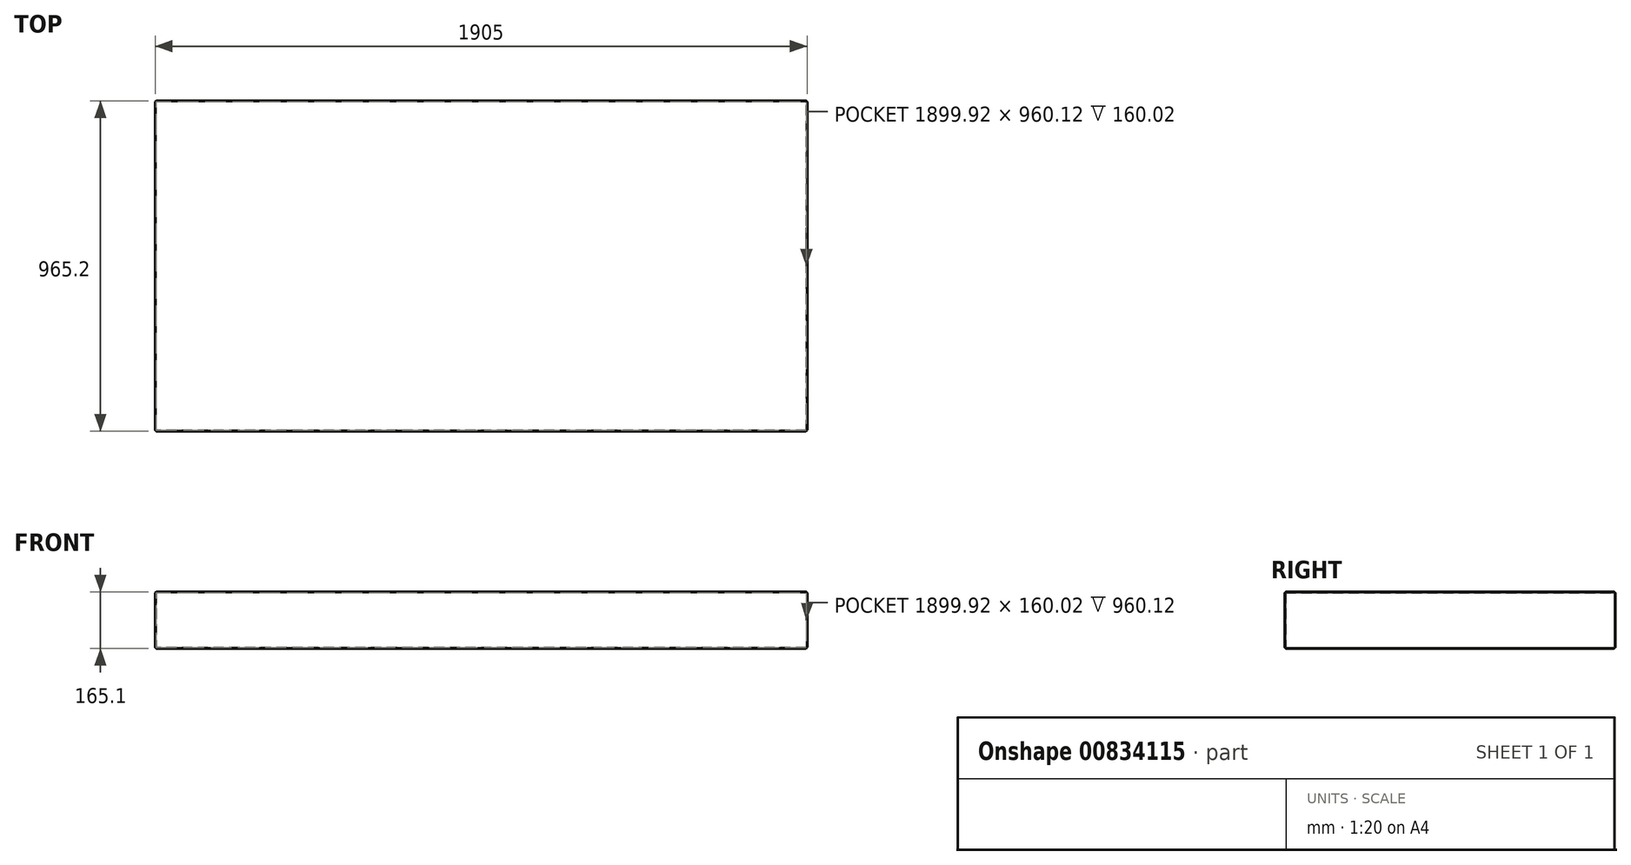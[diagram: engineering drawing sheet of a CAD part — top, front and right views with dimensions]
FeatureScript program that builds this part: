
annotation { "Feature Type Name" : "Feature", "Feature Type Description" : "" }
export const myFeature = defineFeature(function(context is Context, id is Id, definition is map)
    precondition{}
    {
        {
            var Q0;
            Q0=qCreatedBy(makeId("Top.planeOp"),FACE);
            var sketch = newSketch(context, id + "F0", { "sketchPlane" : qUnion([Q0])});
            skLineSegment(sketch, "E0.bottom", {"start": v(952.5, -482.6) * mm, "end": v(-952.5, -482.6) * mm});
            skLineSegment(sketch, "E0.top", {"start": v(952.5, 482.6) * mm, "end": v(-952.5, 482.6) * mm});
            skLineSegment(sketch, "E0.left", {"start": v(952.5, -482.6) * mm, "end": v(952.5, 482.6) * mm});
            skLineSegment(sketch, "E0.right", {"start": v(-952.5, -482.6) * mm, "end": v(-952.5, 482.6) * mm});
            skPoint(sketch, "E0.middle", {"position": v(0, 0) * mm});
            skSolve(sketch);
        }
        {
            var Q0;
            Q0=qSketchRegion(id+"F0",true);
            extrude(context, id + "F1", {"entities" : qUnion([Q0]), "depth" : 165.1 * mm});
        }
        {
            var Q0;
            Q0=makeQuery(id+"F1.opExtrude","SWEPT_FACE",FACE,{"disambiguationData":[OSD([sQuery(id+"F0.wireOp",EDGE,"E0.bottom")])]});
            var Q1;
            Q1=makeQuery(id+"F1.opExtrude","CAP_FACE",FACE,{"disambiguationData":[OSD([sQuery(id+"F0.wireOp",EDGE,"E0.bottom"),sQuery(id+"F0.wireOp",EDGE,"E0.top"),sQuery(id+"F0.wireOp",EDGE,"E0.left"),sQuery(id+"F0.wireOp",EDGE,"E0.right")])],"isStart":false});
            var Q2;
            Q2=makeQuery(id+"F1.opExtrude","SWEPT_BODY",BODY,{"disambiguationData":[OSD([sQuery(id+"F0.wireOp",EDGE,"E0.bottom"),sQuery(id+"F0.wireOp",EDGE,"E0.top"),sQuery(id+"F0.wireOp",EDGE,"E0.left"),sQuery(id+"F0.wireOp",EDGE,"E0.right")])]});
            shell(context, id + "F2", {"isHollow" : true, "entities" : qUnion([Q0, Q1]), "parts" : qUnion([Q2]), "thickness" : 2.54 * mm});
        }
        {
            var Q0;
            Q0=makeQuery(id+"F1.opExtrude","SWEPT_FACE",FACE,{"disambiguationData":[OSD([sQuery(id+"F0.wireOp",EDGE,"E0.bottom")])]});
            var Q1;
            Q1=makeQuery(id+"F1.opExtrude","SWEPT_FACE",FACE,{"disambiguationData":[OSD([sQuery(id+"F0.wireOp",EDGE,"E0.right")])]});
            var Q2;
            Q2=makeQuery(id+"F1.opExtrude","CAP_FACE",FACE,{"disambiguationData":[OSD([sQuery(id+"F0.wireOp",EDGE,"E0.bottom"),sQuery(id+"F0.wireOp",EDGE,"E0.top"),sQuery(id+"F0.wireOp",EDGE,"E0.left"),sQuery(id+"F0.wireOp",EDGE,"E0.right")])],"isStart":false});
            var Q3;
            Q3=makeQuery(id+"F1.opExtrude","CAP_FACE",FACE,{"disambiguationData":[OSD([sQuery(id+"F0.wireOp",EDGE,"E0.bottom"),sQuery(id+"F0.wireOp",EDGE,"E0.top"),sQuery(id+"F0.wireOp",EDGE,"E0.left"),sQuery(id+"F0.wireOp",EDGE,"E0.right")])],"isStart":true});
            var Q4;
            Q4=makeQuery(id+"F1.opExtrude","SWEPT_FACE",FACE,{"disambiguationData":[OSD([sQuery(id+"F0.wireOp",EDGE,"E0.top")])]});
            var Q5;
            Q5=makeQuery(id+"F1.opExtrude","SWEPT_FACE",FACE,{"disambiguationData":[OSD([sQuery(id+"F0.wireOp",EDGE,"E0.left")])]});
            fillet(context, id + "F3", {"entities" : qUnion([Q0, Q1, Q2, Q3, Q4, Q5]), "radius" : 5.08 * mm, "tangentPropagation" : true, "allowEdgeOverflow" : false});
        }
    });
